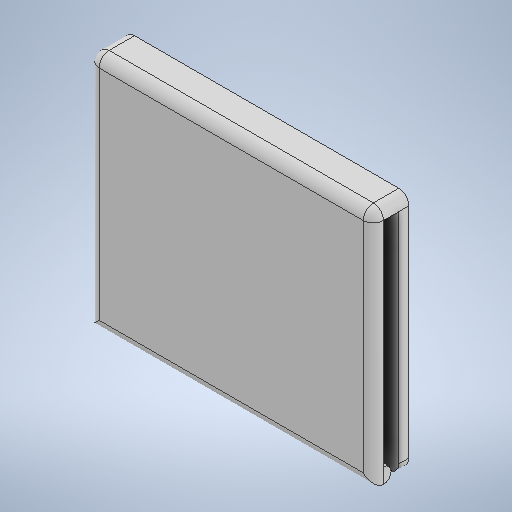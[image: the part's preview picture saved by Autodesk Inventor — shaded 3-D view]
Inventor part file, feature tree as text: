
AUTODESK INVENTOR PART (.ipt)
format: ipt  version: 2025.2 (Build 292293000, 293)  size: 249,344 bytes
history: native  units: mm
features: extrude x2, sketch x2, fillet x1
ambient origin geometry x8: Origin, YZ Plane, XZ Plane, XY Plane, X Axis, Y Axis, Z Axis, Center Point
bodies: Solid1 (feature_tree)
feature tree (5):
  extrude  "Extrusion1"  Depth=45.0mm
  extrude  "Extrusion2"  Depth=47.0mm
  fillet  "Rundung1"  Radius=7.0mm
  sketch  "Sketch1"  dims[d0=2.0mm d1=45.0mm]
  sketch  "Sketch3"  dims[d2=3.0mm d3=47.0mm d4=7.0mm d5=3.0mm d6=1.5mm d7=56.0mm d8=0.0mm d10=135.0deg d11=135.0deg d12=2.8mm d13=28.0mm d14=19.0mm d15=30.0mm d16=0.0mm d17=2.0mm]
